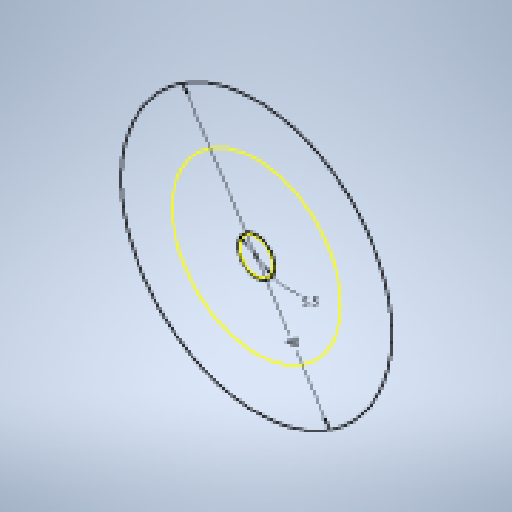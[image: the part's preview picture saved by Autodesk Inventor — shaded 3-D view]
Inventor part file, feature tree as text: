
AUTODESK INVENTOR PART (.ipt)
format: ipt  version: 2023 (Build 270158000, 158)  size: 141,312 bytes
history: native  units: mm
features: other x3, extrude x1, sketch x1, reference x1
ambient origin geometry x8: Origin, YZ Plane, XZ Plane, XY Plane, X Axis, Y Axis, Z Axis, Center Point
bodies: Solid1 (feature_tree)
feature tree (6):
  extrude  "Extrusion1"  Depth=5.0mm
  sketch  "Sketch1"  dims[d0=5.5mm d1=40.0mm d2=5.0mm d3=0.0mm]
  reference  "Reference1"
  other  "<userpath>\OneDrive\Namizje\school\4. letnik\Matura\Izdelovanje\3D model\3D_skenner.iam"
  other  "3D_skenner.iam"
  other  "motor_sample:1"
